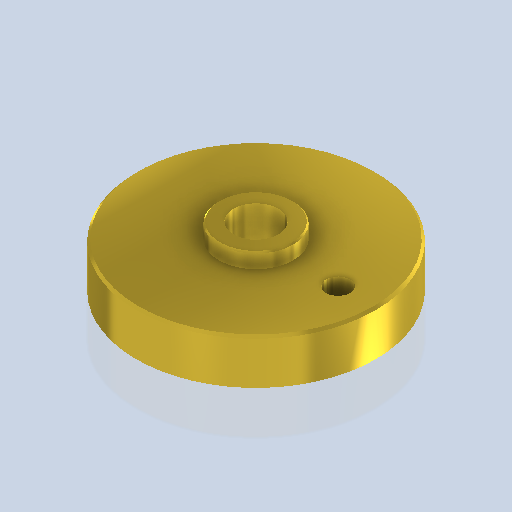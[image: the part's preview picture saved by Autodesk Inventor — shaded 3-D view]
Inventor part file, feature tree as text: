
AUTODESK INVENTOR PART (.ipt)
format: ipt  version: 2024.2 (Build 282272000, 272)  size: 256,512 bytes
history: native  units: mm
features: sketch x4, extrude x2, hole x2, chamfer x2
ambient origin geometry x8: Origin, YZ Plane, XZ Plane, XY Plane, X Axis, Y Axis, Z Axis, Center Point
bodies: Volumenkörper1 (feature_tree)
feature tree (10):
  extrude  "Extrusion1"  Depth=3.0mm TaperAngle=0.0deg
  extrude  "Extrusion2"  Depth=1.0mm TaperAngle=0.0deg
  hole  "Bohrung1"  [1 undecoded]
  hole  "Bohrung2"  [1 undecoded]
  chamfer  "Fasen1"  Distance=0.09mm Angle=45.0deg
  chamfer  "Fasen2"  [1 undecoded]
  sketch  "Skizze1"  dims[d0=16.0mm d1=3.0mm d2=0.0mm]
  sketch  "Skizze2"  dims[d3=5.0mm d4=1.0mm d5=0.0mm]
  sketch  "Skizze3"  dims[d6=3.0mm d7=6.0mm d8=4.0mm d9=2.0mm d10=90.0deg d11=8.0mm d12=20.594885mm]
  sketch  "Skizze4"  dims[d13=1.6mm d14=6.0mm d15=4.0mm d16=2.0mm d17=90.0deg d18=8.0mm d19=20.594885mm d20=5.5mm d21=0.15mm d22=2.0mm d23=45.0deg d24=0.09mm d25=2.0mm d26=45.0deg]
note: 3 required parameter values undecoded (feature->parameter linkage not recoverable at this tier; creation-order binding heuristic only, values carry confidence <= 0.55)
